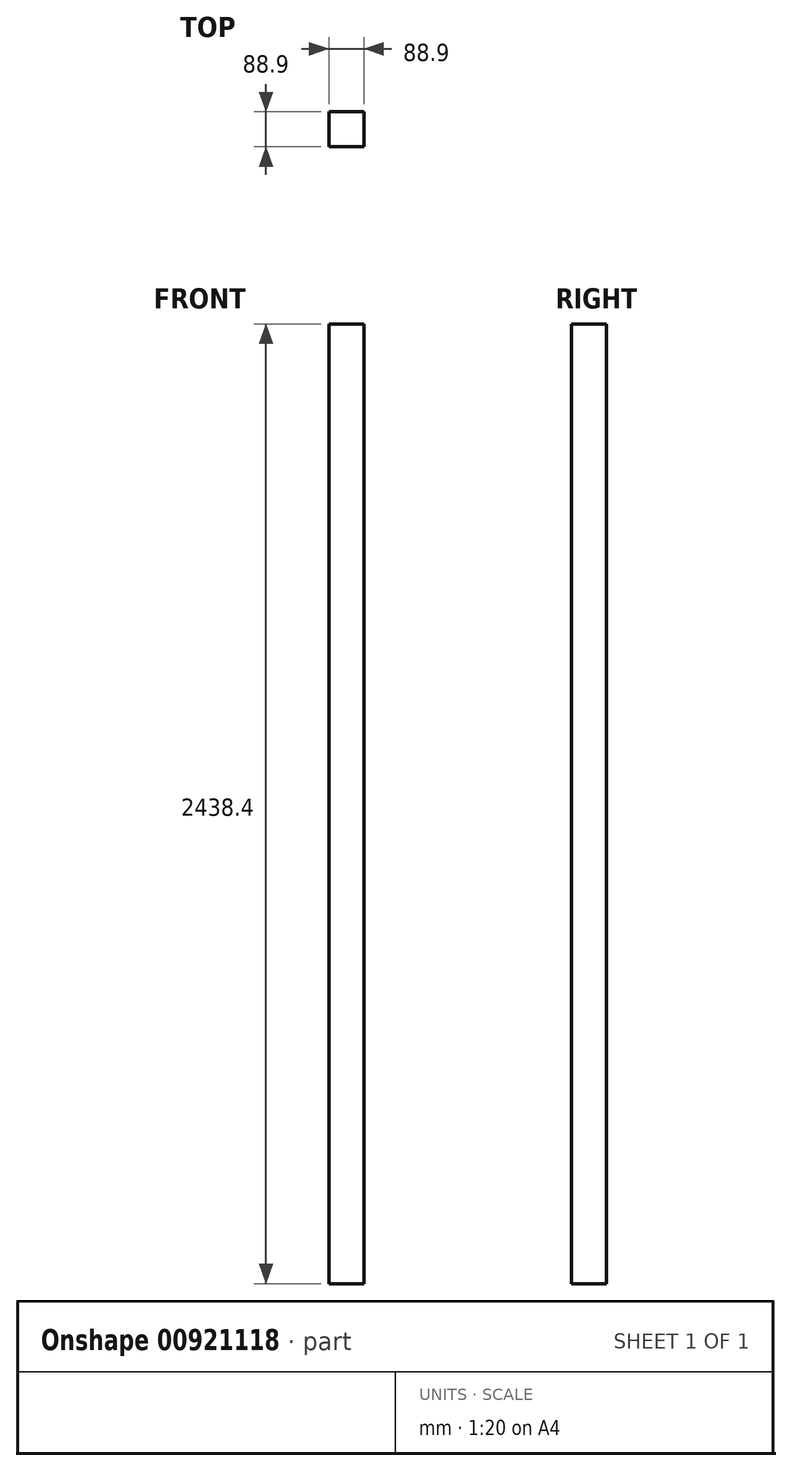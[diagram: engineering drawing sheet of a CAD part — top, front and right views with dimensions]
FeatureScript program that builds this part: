
annotation { "Feature Type Name" : "Feature", "Feature Type Description" : "" }
export const myFeature = defineFeature(function(context is Context, id is Id, definition is map)
    precondition{}
    {
        {
            var Q0;
            Q0=qCreatedBy(makeId("Top.planeOp"),FACE);
            var sketch = newSketch(context, id + "F0", { "sketchPlane" : qUnion([Q0])});
            skLineSegment(sketch, "E0.bottom", {"start": v(0, 0) * mm, "end": v(88.9, 0) * mm});
            skLineSegment(sketch, "E0.top", {"start": v(0, -88.9) * mm, "end": v(88.9, -88.9) * mm});
            skLineSegment(sketch, "E0.left", {"start": v(0, 0) * mm, "end": v(0, -88.9) * mm});
            skLineSegment(sketch, "E0.right", {"start": v(88.9, 0) * mm, "end": v(88.9, -88.9) * mm});
            skSolve(sketch);
        }
        {
            var Q0;
            Q0 = qSketchRegion(id + "F0", true);
            extrude(context, id + "F1", {"entities" : qUnion([Q0]), "depth" : 2438.4 * mm, "offsetDistance" : 25.4 * mm});
        }
    });
